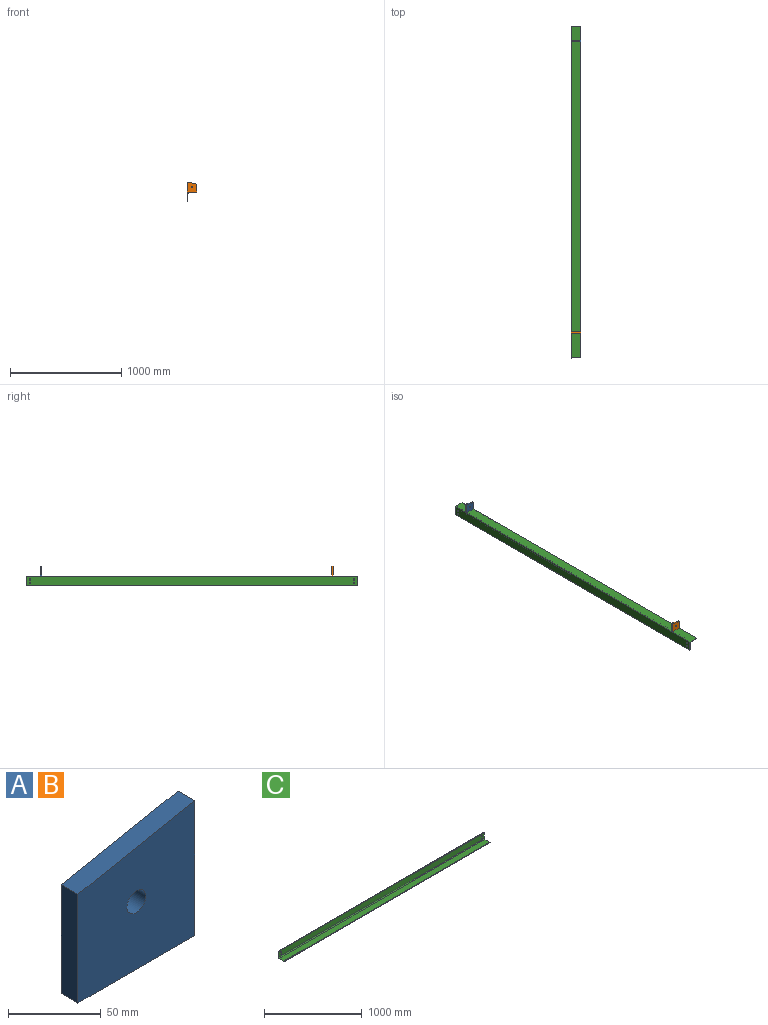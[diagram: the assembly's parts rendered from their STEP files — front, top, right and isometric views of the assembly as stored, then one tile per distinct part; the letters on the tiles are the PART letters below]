
ASSEMBLY  parts=3 mates=2
PART A: 7 faces, bbox 88.9x12.7x88.9 mm
  f0: plane 71.62x12.7mm, normal (-1,0,0), area 909.6mm2, adj f1,f4,f5,f6
  f1: plane 88.9x12.7mm, normal (0,0,-1), area 1129mm2, adj f0,f2,f5,f6
  f2: plane 88.9x12.7mm, normal (1,0,0), area 1129mm2, adj f1,f4,f5,f6
  f3: cylinder r=7.14mm len=14.29mm, axis (0,1,0), area 570mm2, adj f5,f6
  f4: plane 88.9x17.28mm, normal (-0.19,0,0.98), area 1150.2mm2, adj f0,f2,f5,f6
  f5: plane 88.9x88.9mm, normal (0,-1,0), area 6974.8mm2, adj f0,f1,f2,f3,f4
  f6: plane 88.9x88.9mm, normal (0,1,0), area 6974.8mm2, adj f0,f1,f2,f3,f4
PART B: same geometry as A
PART C: 15 faces, bbox 2984.5x88.9x88.9 mm
  f0: plane 88.9x88.9mm, normal (1,0,0), area 1103.8mm2, adj f2,f3,f4,f5,f6,f7,f8,f9
  f1: plane 88.9x88.9mm, normal (-1,0,0), area 1103.8mm2, adj f2,f3,f4,f5,f6,f7,f8,f9
  f2: cylinder r=3.17mm len=2984.5mm, axis (-1,0,0), area 14884.7mm2, adj f0,f1,f3,f10
  f3: plane 2984.5x69.85mm, normal (0,0,1), area 208467.3mm2, adj f0,f1,f2,f4
  f4: cylinder r=9.52mm len=2984.5mm, axis (-1,0,0), area 44654.1mm2, adj f0,f1,f3,f5
  f5: plane 2984.5x69.85mm, normal (0,-1,0), area 207960.6mm2, adj f0,f1,f4,f6,f11,f12,f13,f14
  f6: cylinder r=3.17mm len=2984.5mm, axis (-1,0,0), area 14884.7mm2, adj f0,f1,f5,f7
  f7: plane 2984.5x3.18mm, normal (0,0,1), area 9475.8mm2, adj f0,f1,f6,f8
  f8: plane 2984.5x88.9mm, normal (0,1,0), area 264815.3mm2, adj f0,f1,f7,f9,f11,f12,f13,f14
  f9: plane 2984.5x88.9mm, normal (0,0,-1), area 265322mm2, adj f0,f1,f8,f10
  f10: plane 2984.5x3.18mm, normal (0,-1,0), area 9475.8mm2, adj f0,f1,f2,f9
  f11: cylinder r=6.35mm len=12.7mm, axis (0,1,0), area 253.4mm2, adj f5,f8
  f12: cylinder r=6.35mm len=12.7mm, axis (0,1,0), area 253.4mm2, adj f5,f8
  f13: cylinder r=6.35mm len=12.7mm, axis (0,1,0), area 253.4mm2, adj f5,f8
  f14: cylinder r=6.35mm len=12.7mm, axis (0,1,0), area 253.4mm2, adj f5,f8
PLACE A rot(axis=(0,0,1),180deg) t=(-695.59,7874.37,630.57)mm
PLACE B rot(axis=(0,0,1),180deg) t=(-695.59,5254.99,630.57)mm
PLACE C rot(axis=(0.71,-0.71,0),180deg) t=(-740.04,5032.74,586.12)mm
MATE fastened C.f9 <-> B.f1  axis (0,0,1) through (-695.59,5032.74,586.12)mm
MATE fastened C.f9 <-> A.f1  axis (0,0,1) through (-695.59,8017.24,586.12)mm
